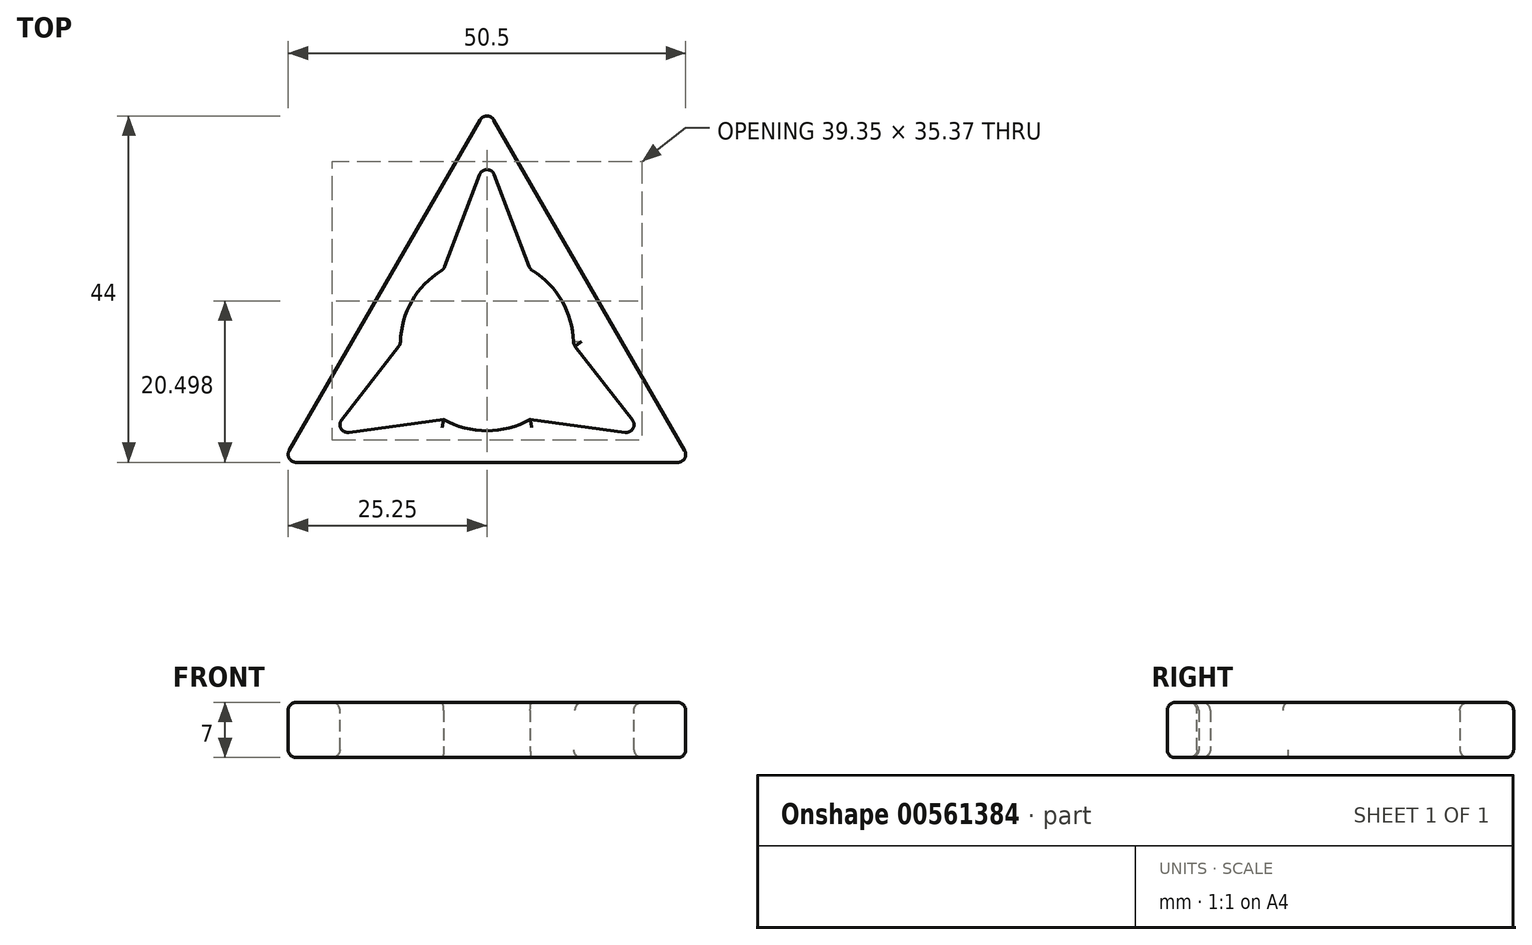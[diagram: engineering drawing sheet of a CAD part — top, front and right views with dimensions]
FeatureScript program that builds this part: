
annotation { "Feature Type Name" : "Feature", "Feature Type Description" : "" }
export const myFeature = defineFeature(function(context is Context, id is Id, definition is map)
    precondition{}
    {
        {
            var Q0;
            Q0=qCreatedBy(makeId("Top.planeOp"),FACE);
            var sketch = newSketch(context, id + "F0", { "sketchPlane" : qUnion([Q0])});
            skCircle(sketch, "E0", {"center": v(0, 0) * mm, "radius": 11 * mm, "construction": true});
            skLineSegment(sketch, "E1", {"start": v(0, 0) * mm, "end": v(0, 30) * mm, "construction": true});
            skLineSegment(sketch, "E2", {"start": v(0, 0) * mm, "end": v(25.98, -15) * mm, "construction": true});
            skLineSegment(sketch, "E3", {"start": v(0, 0) * mm, "end": v(-25.98, -15) * mm, "construction": true});
            skPoint(sketch, "E4", {"position": v(9.53, -5.5) * mm});
            skPoint(sketch, "E5", {"position": v(-9.53, -5.5) * mm});
            skPoint(sketch, "E6", {"position": v(0, 11) * mm});
            skLineSegment(sketch, "E7", {"start": v(0, 0) * mm, "end": v(9.53, 5.5) * mm, "construction": true});
            skLineSegment(sketch, "E8", {"start": v(0, 0) * mm, "end": v(-9.53, 5.5) * mm, "construction": true});
            skLineSegment(sketch, "E9", {"start": v(0, 0) * mm, "end": v(0, -11) * mm, "construction": true});
            skLineSegment(sketch, "E10", {"start": v(0, 30) * mm, "end": v(25.98, -15) * mm});
            skLineSegment(sketch, "E11", {"start": v(25.98, -15) * mm, "end": v(-25.98, -15) * mm});
            skLineSegment(sketch, "E12", {"start": v(-25.98, -15) * mm, "end": v(0, 30) * mm});
            skLineSegment(sketch, "E13", {"start": v(0, 0) * mm, "end": v(5.5, 9.53) * mm, "construction": true});
            skLineSegment(sketch, "E14", {"start": v(0, 0) * mm, "end": v(11, 0) * mm, "construction": true});
            skLineSegment(sketch, "E15", {"start": v(0, 0) * mm, "end": v(-5.5, -9.53) * mm, "construction": true});
            skLineSegment(sketch, "E16", {"start": v(0, 0) * mm, "end": v(5.5, -9.53) * mm, "construction": true});
            skLineSegment(sketch, "E17", {"start": v(0, 0) * mm, "end": v(-11, 0) * mm, "construction": true});
            skLineSegment(sketch, "E18", {"start": v(0, 0) * mm, "end": v(-5.5, 9.53) * mm, "construction": true});
            skLineSegment(sketch, "E19", {"start": v(0, 24) * mm, "end": v(5.5, 9.53) * mm});
            skLineSegment(sketch, "E20", {"start": v(11, 0) * mm, "end": v(19.98, -11.54) * mm});
            skLineSegment(sketch, "E21", {"start": v(19.98, -11.54) * mm, "end": v(5.5, -9.53) * mm});
            skLineSegment(sketch, "E22", {"start": v(0, 24) * mm, "end": v(-5.5, 9.53) * mm});
            skPoint(sketch, "E23.start.orphan", {"position": v(-19.05, -11) * mm});
            skLineSegment(sketch, "E24", {"start": v(-5.5, -9.53) * mm, "end": v(-19.98, -11.54) * mm});
            skLineSegment(sketch, "E25", {"start": v(-19.98, -11.54) * mm, "end": v(-11, 0) * mm});
            skArc(sketch, "E26", {"start": v(5.5, 9.53) * mm, "mid": v(9.53, 5.5) * mm, "end": v(11, 0) * mm});
            skArc(sketch, "E27", {"start": v(-11, 0) * mm, "mid": v(-9.53, 5.5) * mm, "end": v(-5.5, 9.53) * mm});
            skArc(sketch, "E28", {"start": v(-5.5, -9.53) * mm, "mid": v(0, -11) * mm, "end": v(5.5, -9.53) * mm});
            skSolve(sketch);
        }
        {
            var Q0;
            Q0=makeQuery(id+"F0.imprint","IMPRINT",FACE,{"disambiguationData":[TD([[makeQuery(id+"F0.imprint","IMPRINT",EDGE,{"derivedFrom":sQuery(id+"F0.wireOp",EDGE,"E10")}),-1.0]])]});
            extrude(context, id + "F1", {"entities" : qUnion([Q0]), "endBound" : BoundingType.SYMMETRIC, "depth" : 7 * mm, "offsetDistance" : 25.4 * mm});
        }
        {
            var Q0;
            Q0=makeQuery(id+"F1.opExtrude","SWEPT_FACE",FACE,{"disambiguationData":[OSD([sQuery(id+"F0.wireOp",EDGE,"E11")])]});
            var Q1;
            Q1=makeQuery(id+"F1.opExtrude","CAP_FACE",FACE,{"disambiguationData":[OSD([sQuery(id+"F0.wireOp",EDGE,"E10"),sQuery(id+"F0.wireOp",EDGE,"E11"),sQuery(id+"F0.wireOp",EDGE,"E12"),sQuery(id+"F0.wireOp",EDGE,"E19"),sQuery(id+"F0.wireOp",EDGE,"E20"),sQuery(id+"F0.wireOp",EDGE,"E21"),sQuery(id+"F0.wireOp",EDGE,"E22"),sQuery(id+"F0.wireOp",EDGE,"E24"),sQuery(id+"F0.wireOp",EDGE,"E25"),sQuery(id+"F0.wireOp",EDGE,"E26"),sQuery(id+"F0.wireOp",EDGE,"E27"),sQuery(id+"F0.wireOp",EDGE,"E28")])],"isStart":false});
            var Q2;
            Q2=makeQuery(id+"F1.opExtrude","SWEPT_FACE",FACE,{"disambiguationData":[OSD([sQuery(id+"F0.wireOp",EDGE,"E25")])]});
            var Q3;
            Q3=makeQuery(id+"F1.opExtrude","SWEPT_FACE",FACE,{"disambiguationData":[OSD([sQuery(id+"F0.wireOp",EDGE,"E22")])]});
            var Q4;
            Q4=makeQuery(id+"F1.opExtrude","SWEPT_FACE",FACE,{"disambiguationData":[OSD([sQuery(id+"F0.wireOp",EDGE,"E19")])]});
            var Q5;
            Q5=makeQuery(id+"F1.opExtrude","SWEPT_FACE",FACE,{"disambiguationData":[OSD([sQuery(id+"F0.wireOp",EDGE,"E26")])]});
            var Q6;
            Q6=makeQuery(id+"F1.opExtrude","SWEPT_FACE",FACE,{"disambiguationData":[OSD([sQuery(id+"F0.wireOp",EDGE,"E20")])]});
            var Q7;
            Q7=makeQuery(id+"F1.opExtrude","CAP_FACE",FACE,{"disambiguationData":[OSD([sQuery(id+"F0.wireOp",EDGE,"E10"),sQuery(id+"F0.wireOp",EDGE,"E11"),sQuery(id+"F0.wireOp",EDGE,"E12"),sQuery(id+"F0.wireOp",EDGE,"E19"),sQuery(id+"F0.wireOp",EDGE,"E20"),sQuery(id+"F0.wireOp",EDGE,"E21"),sQuery(id+"F0.wireOp",EDGE,"E22"),sQuery(id+"F0.wireOp",EDGE,"E24"),sQuery(id+"F0.wireOp",EDGE,"E25"),sQuery(id+"F0.wireOp",EDGE,"E26"),sQuery(id+"F0.wireOp",EDGE,"E27"),sQuery(id+"F0.wireOp",EDGE,"E28")])],"isStart":true});
            var Q8;
            Q8=makeQuery(id+"F1.opExtrude","SWEPT_EDGE",EDGE,{"disambiguationData":[OSD([sQuery(id+"F0.wireOp",EDGE,"E10"),sQuery(id+"F0.wireOp",EDGE,"E12")])]});
            fillet(context, id + "F2", {"entities" : qUnion([Q0, Q1, Q2, Q3, Q4, Q5, Q6, Q7, Q8]), "radius" : 1 * mm, "tangentPropagation" : true, "allowEdgeOverflow" : false});
        }
    });
